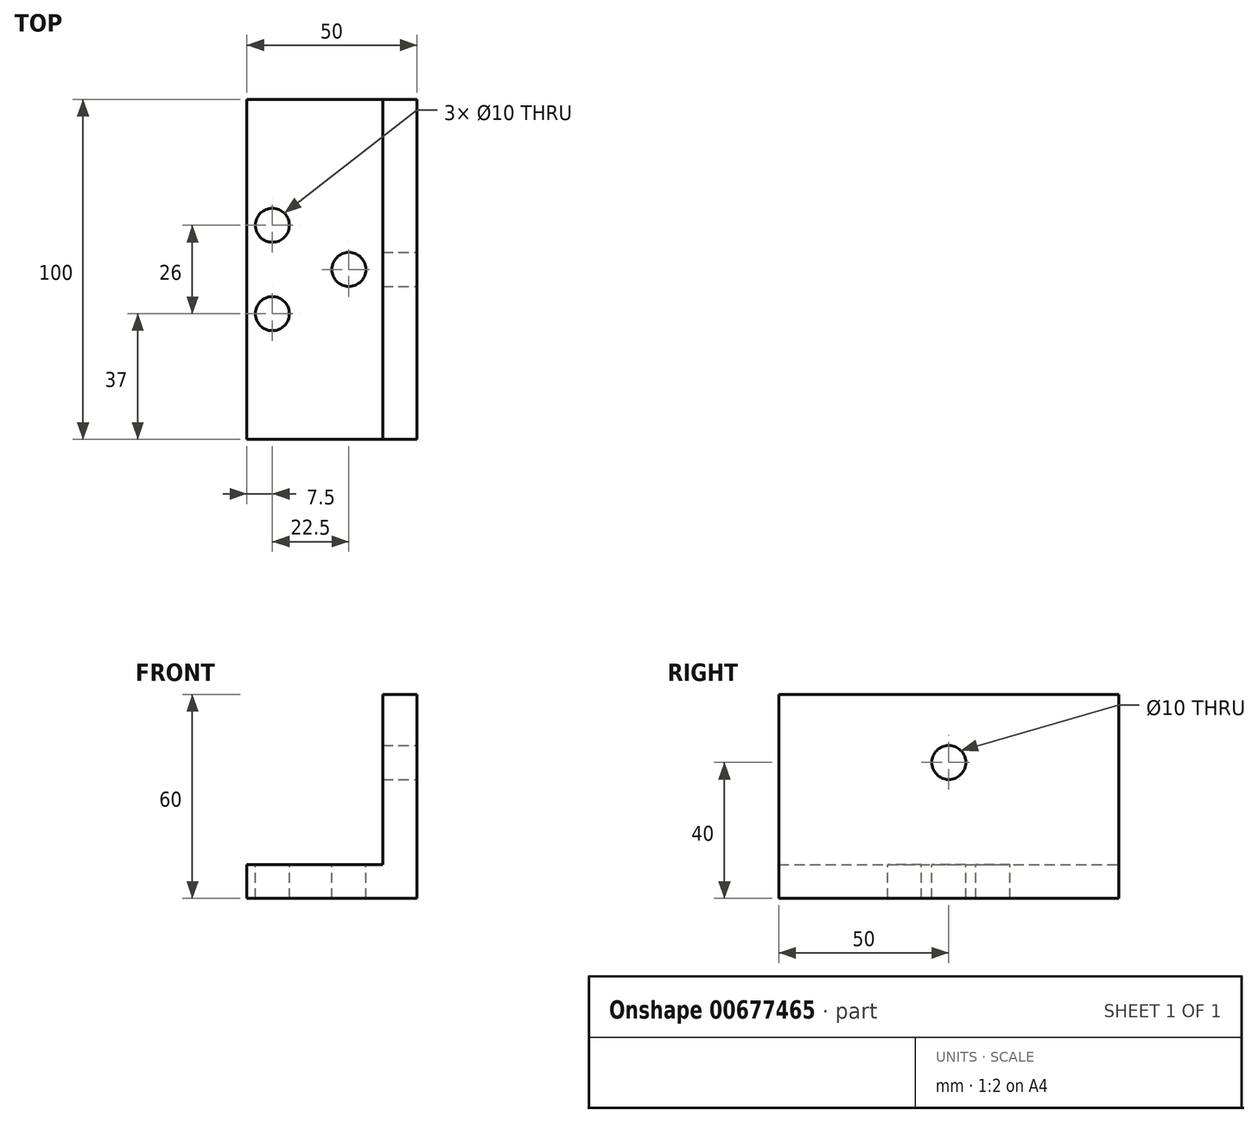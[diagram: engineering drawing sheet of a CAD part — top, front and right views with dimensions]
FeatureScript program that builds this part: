
annotation { "Feature Type Name" : "Feature", "Feature Type Description" : "" }
export const myFeature = defineFeature(function(context is Context, id is Id, definition is map)
    precondition{}
    {
        {
            var Q0;
            Q0=qCreatedBy(makeId("Front.planeOp"),FACE);
            var sketch = newSketch(context, id + "F0", { "sketchPlane" : qUnion([Q0])});
            skLineSegment(sketch, "E0", {"start": v(0, 0) * mm, "end": v(50, 0) * mm});
            skLineSegment(sketch, "E1", {"start": v(50, 0) * mm, "end": v(50, 60) * mm});
            skLineSegment(sketch, "E2", {"start": v(50, 60) * mm, "end": v(40, 60) * mm});
            skLineSegment(sketch, "E3", {"start": v(40, 60) * mm, "end": v(40, 10) * mm});
            skLineSegment(sketch, "E4", {"start": v(40, 10) * mm, "end": v(0, 10) * mm});
            skLineSegment(sketch, "E5", {"start": v(0, 10) * mm, "end": v(0, 0) * mm});
            skSolve(sketch);
        }
        {
            var Q0;
            Q0=makeQuery(id+"F0.imprint","IMPRINT",FACE,{"disambiguationData":[TD([[makeQuery(id+"F0.imprint","IMPRINT",EDGE,{"derivedFrom":sQuery(id+"F0.wireOp",EDGE,"E0")}),1.0]])]});
            extrude(context, id + "F1", {"entities" : qUnion([Q0]), "depth" : 100 * mm, "offsetDistance" : 25 * mm, "symmetric" : true});
        }
        {
            var Q0;
            Q0=makeQuery(id+"F1.opExtrude","SWEPT_FACE",FACE,{"disambiguationData":[OSD([sQuery(id+"F0.wireOp",EDGE,"E1")])]});
            var sketch = newSketch(context, id + "F2", { "sketchPlane" : qUnion([Q0])});
            skCircle(sketch, "E6", {"center": v(0, 40) * mm, "radius": 5 * mm});
            skSolve(sketch);
        }
        {
            var Q0;
            Q0 = qSketchRegion(id + "F2", true);
            extrude(context, id + "F3", {"entities" : qUnion([Q0]), "operationType" : NewBodyOperationType.REMOVE, "endBound" : BoundingType.UP_TO_NEXT, "oppositeDirection" : true, "depth" : 25 * mm, "offsetDistance" : 25 * mm});
        }
        {
            var Q0;
            Q0=makeQuery(id+"F1.opExtrude","SWEPT_FACE",FACE,{"disambiguationData":[OSD([sQuery(id+"F0.wireOp",EDGE,"E4")])]});
            var sketch = newSketch(context, id + "F4", { "sketchPlane" : qUnion([Q0])});
            skCircle(sketch, "E7", {"center": v(30, 0) * mm, "radius": 5 * mm});
            skLineSegment(sketch, "E8", {"start": v(7.5, 24.03) * mm, "end": v(7.5, -24.74) * mm, "construction": true});
            skCircle(sketch, "E9", {"center": v(7.5, 13) * mm, "radius": 5 * mm});
            skLineSegment(sketch, "E10", {"start": v(40.67, 0) * mm, "end": v(-11.83, 0) * mm, "construction": true});
            skCircle(sketch, "E11.MirrorC", {"center": v(7.5, -13) * mm, "radius": 5 * mm});
            skSolve(sketch);
        }
        {
            var Q0;
            Q0 = qSketchRegion(id + "F4", true);
            extrude(context, id + "F5", {"entities" : qUnion([Q0]), "operationType" : NewBodyOperationType.REMOVE, "endBound" : BoundingType.UP_TO_NEXT, "oppositeDirection" : true, "depth" : 25 * mm, "offsetDistance" : 25 * mm});
        }
    });
